# Revit family: Sanitary_Toilets_hansgrohe_22431CHN-MitaPura-S-Floorstanding-WC-one
name_source: partatom
category: Plumbing Fixtures
revit_build: Autodesk Revit 2018 (Build: 20190510_1515(x64)
units: mm (PartAtom-declared; Revit-internal decimal feet)

## family parameters
Always vertical = No
Cut with Voids When Loaded = No
OmniClass Number = 23.31.19.00
OmniClass Title = Toilets
Part Type = Normal
Room Calculation Point = No
Round Connector Dimension = Use Diameter
Shared = No
Work Plane-Based = Yes

## types (1)
- Sanitary_Toilets_hansgrohe_22431CHN-MitaPura-S-Floorstanding-WC-one
    Always visible = Yes
    BIMobject category = Toilets
    Default Elevation = 1219.2 mm  [stored 4 ft]
    Description = MitaPura S Floorstanding WC one piece with vertical outlet 305 rimless
    Design country = Germany
    EAN code = 4059625384893
    Edition number = 1
    GTIN code = https://4059625384893
    IFC Classification = Sanitary Terminal
    Manufacturer = Hansgrohe
    Manufacturer country = Germany
    Manufacturer name = hansgrohe
    Material = Hansgrohe - Ceramic - 007 White
    Material main = Ceramics
    Model = 22431CHN MitaPura S Floorstanding WC one piece with vertical outlet 305 rimless
    OmniClass Code = 23-31 19 00
    OmniClass Description = Toilets
    Product Guid = 55fa705e-f251-4c88-afb4-eb1da0b4fedb
    Product SKU = 22431CHN
    Product data url = https://bimobject.com
    Product family = MitaPura S
    Product group = toilet combinations
    Product name = 22431CHN MitaPura S Floorstanding WC one piece with vertical outlet 305 rimless
    QR code = https://bimobject.com
    URL = https://www.hansgrohe.com
    Water Inlet = 12.7 mm  [stored 0.0416667 ft]
    Water Inlet Description = Water Inlet 1/2''
    Water Outlet = 102 mm
    Water Outlet Description = Water Outlet 102mm
    Weight Net (Kg) = 53.7

note: [stored X ft] marks values corroborated as IEEE doubles in the binary element streams (Revit-internal decimal feet)

## geometry (parser evidence)
native form markers: Sweep x3
no freeform markers — native parametric forms only
